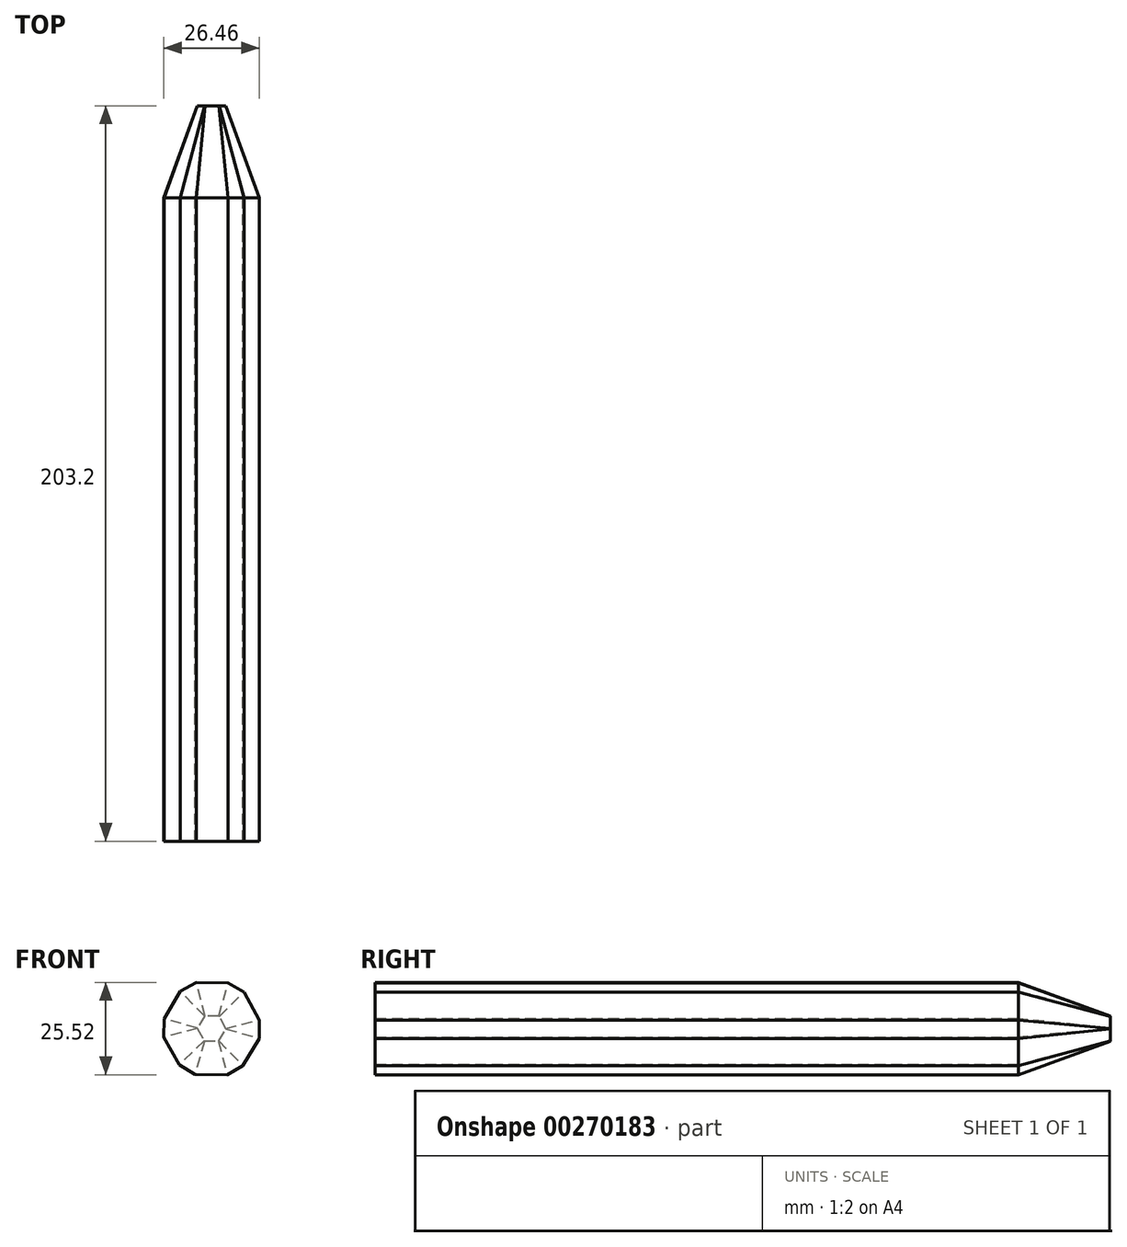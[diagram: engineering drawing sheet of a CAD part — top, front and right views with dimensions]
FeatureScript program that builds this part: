
annotation { "Feature Type Name" : "Feature", "Feature Type Description" : "" }
export const myFeature = defineFeature(function(context is Context, id is Id, definition is map)
    precondition{}
    {
        {
            var Q0;
            Q0=qCreatedBy(makeId("Front.planeOp"),FACE);
            var sketch = newSketch(context, id + "F0", { "sketchPlane" : qUnion([Q0])});
            skCircle(sketch, "E0.cCircle", {"center": v(0, 0) * mm, "radius": 12.7 * mm, "construction": true});
            skLineSegment(sketch, "E0.0", {"start": v(7.5, 12.6) * mm, "end": v(14.66, -0.2) * mm});
            skLineSegment(sketch, "E0.1", {"start": v(14.66, -0.2) * mm, "end": v(7.16, -12.8) * mm});
            skLineSegment(sketch, "E0.2", {"start": v(7.16, -12.8) * mm, "end": v(-7.5, -12.6) * mm});
            skLineSegment(sketch, "E0.3", {"start": v(-7.5, -12.6) * mm, "end": v(-14.66, 0.2) * mm});
            skLineSegment(sketch, "E0.4", {"start": v(-14.66, 0.2) * mm, "end": v(-7.16, 12.8) * mm});
            skLineSegment(sketch, "E0.5", {"start": v(-7.16, 12.8) * mm, "end": v(7.5, 12.6) * mm});
            skPoint(sketch, "E0.0.midPoint", {"position": v(11.08, 6.2) * mm});
            skSolve(sketch);
        }
        {
            var Q0;
            Q0 = qSketchRegion(id + "F0", true);
            extrude(context, id + "F1", {"entities" : qUnion([Q0]), "endBound" : BoundingType.SYMMETRIC, "depth" : 177.8 * mm});
        }
        {
            var Q0;
            Q0=makeQuery(id+"F1.opExtrude","SWEPT_EDGE",EDGE,{"disambiguationData":[OSD([sQuery(id+"F0.wireOp",EDGE,"E0.0"),sQuery(id+"F0.wireOp",EDGE,"E0.1")])]});
            var Q1;
            Q1=makeQuery(id+"F1.opExtrude","SWEPT_EDGE",EDGE,{"disambiguationData":[OSD([sQuery(id+"F0.wireOp",EDGE,"E0.0"),sQuery(id+"F0.wireOp",EDGE,"E0.5")])]});
            var Q2;
            Q2=makeQuery(id+"F1.opExtrude","SWEPT_EDGE",EDGE,{"disambiguationData":[OSD([sQuery(id+"F0.wireOp",EDGE,"E0.4"),sQuery(id+"F0.wireOp",EDGE,"E0.5")])]});
            var Q3;
            Q3=makeQuery(id+"F1.opExtrude","SWEPT_EDGE",EDGE,{"disambiguationData":[OSD([sQuery(id+"F0.wireOp",EDGE,"E0.3"),sQuery(id+"F0.wireOp",EDGE,"E0.4")])]});
            var Q4;
            Q4=makeQuery(id+"F1.opExtrude","SWEPT_EDGE",EDGE,{"disambiguationData":[OSD([sQuery(id+"F0.wireOp",EDGE,"E0.2"),sQuery(id+"F0.wireOp",EDGE,"E0.3")])]});
            var Q5;
            Q5=makeQuery(id+"F1.opExtrude","SWEPT_EDGE",EDGE,{"disambiguationData":[OSD([sQuery(id+"F0.wireOp",EDGE,"E0.1"),sQuery(id+"F0.wireOp",EDGE,"E0.2")])]});
            chamfer(context, id + "F2", {"entities" : qUnion([Q0, Q1, Q2, Q3, Q4, Q5]), "width" : 5.08 * mm, "tangentPropagation" : true});
        }
        {
            var Q0;
            Q0=makeQuery(id+"F1.opExtrude","CAP_FACE",FACE,{"disambiguationData":[OSD([sQuery(id+"F0.wireOp",EDGE,"E0.0"),sQuery(id+"F0.wireOp",EDGE,"E0.1"),sQuery(id+"F0.wireOp",EDGE,"E0.2"),sQuery(id+"F0.wireOp",EDGE,"E0.3"),sQuery(id+"F0.wireOp",EDGE,"E0.4"),sQuery(id+"F0.wireOp",EDGE,"E0.5")])],"isStart":true});
            extrude(context, id + "F3", {"entities" : qUnion([Q0]), "operationType" : NewBodyOperationType.ADD, "depth" : 25.4 * mm, "hasDraft" : true, "draftAngle" : 20 * degree, "draftPullDirection" : true});
        }
    });
